# Revit family: xBathtub-American_Standard-Townsend-2691.004
name_source: partatom
category: Plumbing Fixtures
revit_build: Autodesk Revit 2014 (Build: 20130308_1515(x64)
units: mm (PartAtom-declared; Revit-internal decimal feet)

## types (1)
- 2691.004
    Assembly Code = D2010510
    CW Connection = Yes
    CWFU = 3
    Default Elevation = 0"
    Description = American Standard Townsend Freestanding Tub
    HW Connection = Yes
    HWFU = 3
    Height = 24"
    Installation Type = Freestanding
    Length = 67 15/16"
    Manufacturer = American Standard
    Material = High Gloss Acrylic-American Standard-020-White
    Model = 2691.004
    Price = Prices may vary. Please consult Manufacturer Representative for most up-to-date price list.
    Product Documentation Link = https://www.americanstandard-us.com
    Product Page URL = https://www.americanstandard-us.com
    Shipping Weight = 150 lb
    Type Comments = Straight back wall allows for a flush-to-the-wall installation.
    URL = https://www.americanstandard-us.com
    Vent Connection = No
    WFU = 4
    Warranty Information = Limited Lifetime Warranty. 3 Years Commercial.
    Waste Connection = Yes
    Waste Connection Diameter = 2 3/16"
    Waste Connection Radius = 1 3/32"
    Width = 36"

## geometry (parser evidence)
native form markers: Sweep x1
no freeform markers — native parametric forms only
